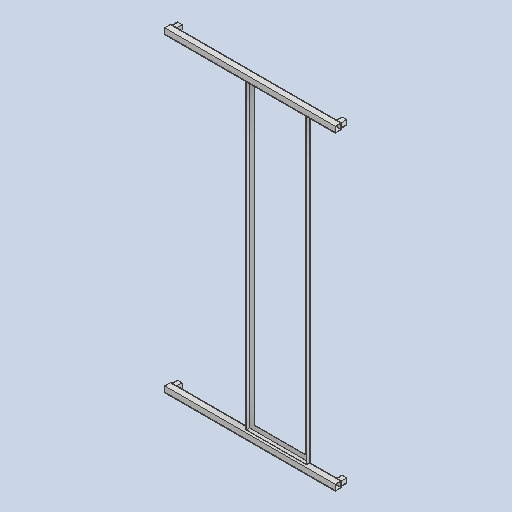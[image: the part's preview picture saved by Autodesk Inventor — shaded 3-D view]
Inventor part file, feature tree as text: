
AUTODESK INVENTOR PART (.ipt)
format: ipt  version: 2025 (Build 290162000, 162)  size: 180,736 bytes
history: native  units: mm
features: extrude x3, shell x3, projected_geometry x2, sketch x1
ambient origin geometry x8: Origin, YZ Plane, XZ Plane, XY Plane, X Axis, Y Axis, Z Axis, Center Point
bodies: Solid1 (feature_tree), Solid2 (feature_tree), Solid3 (feature_tree)
feature tree (9):
  extrude  "Extrusion1"  Depth=2605.0mm
  extrude  "Extrusion2"  Depth=50.0mm
  shell  "Shell1"  Thickness=500.0mm
  shell  "Shell2"  Thickness=2505.0mm
  extrude  "Extrusion3"  Depth=50.0mm
  shell  "Shell3"  Thickness=40.0mm
  projected_geometry  "Projected Loop1"
  projected_geometry  "Projected Loop2"
  sketch  "Sketch Rectangular Pattern1"  dims[d0=1405.0mm d1=2605.0mm d2=50.0mm d3=500.0mm d4=2505.0mm d5=600.0mm d6=40.0mm d7=50.0mm d8=0.0mm d9=30.0mm d10=0.0mm d11=3.0mm d12=3.0mm d13=50.0mm d14=50.0mm d15=5.0mm d16=20.0mm d18=2556.0mm d19=20.0mm d21=1356.0mm d24=50.0mm d25=0.0mm d26=3.0mm d27=50.0mm]
